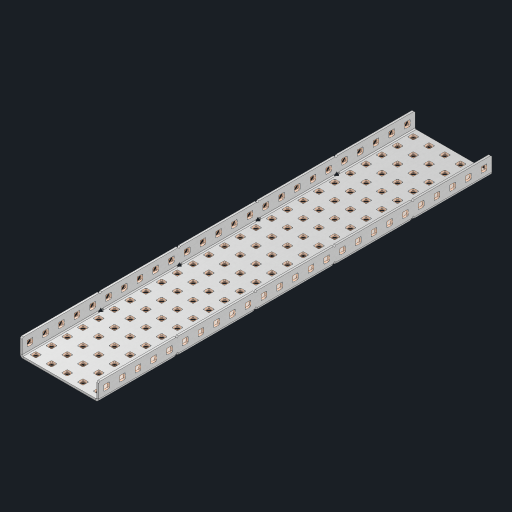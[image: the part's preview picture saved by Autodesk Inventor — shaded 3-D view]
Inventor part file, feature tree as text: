
AUTODESK INVENTOR PART (.ipt)
format: ipt  version: 2023 (Build 270158000, 158)  size: 1,938,432 bytes
history: native  units: in
note: dims shown in document units (in); Inventor stores cm internally (conversion verified against a paired STEP export)
features: other x180, extrude x174, sheet_metal_op x10, sketch x8, mirror x1, pattern_linear x1, chamfer x1
ambient origin geometry x8: Origin, YZ Plane, XZ Plane, XY Plane, X Axis, Y Axis, Z Axis, Center Point
bodies: Solid1 (feature_tree), Body (feature_tree)
feature tree (375):
  other  "Flange Pattern Plane"
  sheet_metal_op  "Flange Pattern"
  sheet_metal_op  "Body Pattern"
  other  "Arc Length"
  mirror  "Notch Mirror"
  pattern_linear  "Notch Pattern"  Spacing1=0.25in  [1 undecoded]
  chamfer  "End Chamfer"
  extrude  "Half Cut"  Depth=0.0625in
  sketch  "Sketch1"  dims[d0=2.5in]
  other  "Plate1"
  sketch  "Sketch2"  dims[d1=12.5in]
  other  "Plate2"
  sheet_metal_op  "Bend1"
  sheet_metal_op  "Corner1"
  sketch  "Sketch3"  dims[d2=0.0625in]
  other  "Flange Pattern Sketch"
  sketch  "Sketch7"  dims[d3=0.0625in]
  other  "Srf1"
  other  "Srf2"
  sketch  "Sketch8"  dims[d4=0.0312in]
  sketch  "Sketch9"  dims[d5=0.125in]
  other  "Srf91"
  sheet_metal_op  "Body Pattern Sketch"
  other  "Srf92"
  sketch  "Sketch13"  dims[d6=0.0625in]
  sketch  "Sketch14"  dims[d7=0.5in d8=90.0deg d9=0.0312in d10=0.25in d11=0.0625in d12=0.0625in d16=0.182in d17=0.02in d18=0.0625in d19=0.0in d20=0.25in d21=0.25in d46=0.172in d47=1.0in d48=0.0in d49=0.182in d50=0.02in d51=0.25in d52=0.25in d53=0.0625in d54=0.0in d55=0.172in d56=1.0in d57=0.0in d60=9.8425in d62=0.5in d63=1.9685in d65=0.5in d85=0.1473in d86=0.1782in d88=0.04in d89=0.0625in d90=0.0in d91=0.04in d92=0.0491in d95=2.5in d96=0.04in d97=0.25in d98=45.0deg d101=0.0in d102=2.497in d131=2.5in d132=9.8425in d134=0.5in d139=0.5in]
  other  "Srf856"
  other  "Srf1310"
  other  "Srf1311"
  other  "Srf1312"
  other  "Srf1376"
  other  "Srf1377"
  other  "Srf1728"
  other  "Srf1755"
  other  "Srf1878"
  other  "Srf1879"
  other  "Srf1880"
  other  "Srf1881"
  other  "Srf1882"
  other  "Srf1883"
  other  "Srf1884"
  other  "Srf1885"
  other  "Srf1886"
  other  "Srf1887"
  other  "Srf1888"
  other  "Srf1889"
  other  "Srf1890"
  other  "Srf1891"
  other  "Srf1892"
  other  "Srf1893"
  other  "Srf1894"
  other  "Srf1895"
  other  "Srf1896"
  other  "Srf1897"
  other  "Srf1898"
  other  "Srf1899"
  other  "Srf1900"
  other  "Srf1901"
  other  "Srf1902"
  other  "Srf1903"
  other  "Srf1904"
  other  "Srf1905"
  other  "Srf1906"
  other  "Srf1942"
  other  "Srf1943"
  other  "Srf1944"
  other  "Srf1945"
  other  "Srf1946"
  other  "Srf1947"
  other  "Srf1948"
  other  "Srf1949"
  other  "Srf1950"
  other  "Srf1951"
  other  "Srf1952"
  other  "Srf1953"
  other  "Srf1954"
  other  "Srf1955"
  other  "Srf1956"
  other  "Srf1957"
  other  "Srf1958"
  other  "Srf1959"
  other  "Srf1960"
  other  "Srf1961"
  other  "Srf1962"
  other  "Srf1963"
  other  "Srf1964"
  other  "Srf1965"
  other  "Srf1966"
  other  "Srf1967"
  other  "Srf1968"
  other  "Srf1969"
  other  "Srf1970"
  other  "Srf2111"
  other  "Srf2112"
  other  "Srf2113"
  other  "Srf2114"
  other  "Srf2115"
  other  "Srf2116"
  other  "Srf2117"
  other  "Srf2118"
  other  "Srf2119"
  other  "Srf2120"
  other  "Srf2121"
  other  "Srf2122"
  other  "Srf2123"
  other  "Srf2124"
  other  "Srf2125"
  other  "Srf2146"
  other  "Srf2147"
  other  "Srf2148"
  other  "Srf2149"
  other  "Srf2150"
  other  "Srf2151"
  other  "Srf2152"
  other  "Srf2153"
  other  "Srf2154"
  other  "Srf2155"
  other  "Srf2156"
  other  "Srf2157"
  other  "Srf2158"
  other  "Srf2159"
  other  "Srf2160"
  other  "Srf2161"
  other  "Srf2162"
  other  "Srf2163"
  other  "Srf2164"
  other  "Srf2165"
  other  "Srf2166"
  other  "Srf2167"
  other  "Srf2168"
  other  "Srf2169"
  other  "Srf2170"
  other  "Srf2171"
  other  "Srf2172"
  other  "Srf2173"
  other  "Srf2174"
  other  "Srf2175"
  other  "Srf2176"
  other  "Srf2177"
  other  "Srf2178"
  other  "Srf2179"
  other  "Srf2180"
  other  "Srf2181"
  other  "Srf2182"
  other  "Srf2183"
  other  "Srf2184"
  other  "Srf2185"
  other  "Srf2186"
  other  "Srf2187"
  other  "Srf2188"
  other  "Srf2189"
  other  "Srf2190"
  other  "Srf2191"
  other  "Srf2192"
  other  "Srf2193"
  other  "Srf2194"
  other  "Srf2195"
  other  "Srf2196"
  other  "Srf2197"
  other  "Srf2198"
  other  "Srf2199"
  other  "Srf2200"
  other  "Srf2201"
  other  "Srf2202"
  other  "Srf2203"
  other  "Srf2204"
  other  "Srf2205"
  other  "Srf2206"
  other  "Srf2207"
  other  "Srf2208"
  other  "Srf2209"
  other  "Srf2210"
  other  "Srf2211"
  other  "Srf2212"
  other  "Srf2213"
  other  "Srf2214"
  other  "Srf2215"
  other  "Srf2216"
  other  "Srf2217"
  other  "Srf2218"
  other  "Srf2219"
  other  "Srf2220"
  other  "Srf2221"
  other  "Srf2222"
  other  "Srf2223"
  other  "Srf2224"
  other  "Srf2225"
  other  "Srf2226"
  other  "Srf2227"
  other  "Srf2228"
  other  "Srf2229"
  other  "Srf2230"
  other  "Srf2231"
  other  "Srf2232"
  other  "Srf2233"
  other  "Srf2234"
  other  "Srf2235"
  sheet_metal_op  "Flange Stamp"
  sheet_metal_op  "Flange Circle"
  sheet_metal_op  "Body Stamp"
  sheet_metal_op  "Body Circle"
  sheet_metal_op  "Notch"
  extrude  "ExtrusionSrf2"  Depth=0.0625in
  extrude  "ExtrusionSrf92"  Depth=2.5in
  extrude  "ExtrusionSrf856"  Depth=0.02in
  extrude  "ExtrusionSrf1310"  Depth=0.0625in
  extrude  "ExtrusionSrf1311"  TaperAngle=0.0deg  [1 undecoded]
  extrude  "ExtrusionSrf1312"  Depth=0.25in
  extrude  "ExtrusionSrf1376"  Depth=0.25in
  extrude  "ExtrusionSrf1377"  Depth=2.5in
  extrude  "ExtrusionSrf1728"  Depth=2.5in TaperAngle=0.0deg
  extrude  "ExtrusionSrf1755"  Depth=2.5in
  extrude  "ExtrusionSrf1878"  Depth=0.02in
  extrude  "ExtrusionSrf1879"  Depth=0.25in
  extrude  "ExtrusionSrf1880"  Depth=0.25in
  extrude  "ExtrusionSrf1881"  Depth=0.0625in
  extrude  "ExtrusionSrf1882"  TaperAngle=0.0deg  [1 undecoded]
  extrude  "ExtrusionSrf1883"  Depth=2.5in
  extrude  "ExtrusionSrf1884"  Depth=2.5in TaperAngle=0.0deg
  extrude  "ExtrusionSrf1885"  Depth=2.5in
  extrude  "ExtrusionSrf1886"  Depth=2.5in
  extrude  "ExtrusionSrf1887"  Depth=2.5in
  extrude  "ExtrusionSrf1888"  Depth=2.5in
  extrude  "ExtrusionSrf1889"  Depth=2.5in
  extrude  "ExtrusionSrf1890"  Depth=0.0625in
  extrude  "ExtrusionSrf1891"  TaperAngle=0.0deg  [1 undecoded]
  extrude  "ExtrusionSrf1892"  Depth=2.5in
  extrude  "ExtrusionSrf1893"  Depth=2.5in
  extrude  "ExtrusionSrf1894"  Depth=2.5in
  extrude  "ExtrusionSrf1895"  Depth=0.25in TaperAngle=45.0deg
  extrude  "ExtrusionSrf1896"  TaperAngle=0.0deg  [1 undecoded]
  extrude  "ExtrusionSrf1897"  Depth=2.5in
  extrude  "ExtrusionSrf1898"  Depth=2.5in
  extrude  "ExtrusionSrf1899"  Depth=2.5in
  extrude  "ExtrusionSrf1900"  Depth=2.5in
  extrude  "ExtrusionSrf1901"  Depth=2.5in
  extrude  "ExtrusionSrf1902"  [1 undecoded]
  extrude  "ExtrusionSrf1903"  [1 undecoded]
  extrude  "ExtrusionSrf1904"  [1 undecoded]
  extrude  "ExtrusionSrf1905"  [1 undecoded]
  extrude  "ExtrusionSrf1906"  [1 undecoded]
  extrude  "ExtrusionSrf1942"  [1 undecoded]
  extrude  "ExtrusionSrf1943"  [1 undecoded]
  extrude  "ExtrusionSrf1944"  [1 undecoded]
  extrude  "ExtrusionSrf1945"  [1 undecoded]
  extrude  "ExtrusionSrf1946"  [1 undecoded]
  extrude  "ExtrusionSrf1947"  [1 undecoded]
  extrude  "ExtrusionSrf1948"  [1 undecoded]
  extrude  "ExtrusionSrf1949"  [1 undecoded]
  extrude  "ExtrusionSrf1950"  [1 undecoded]
  extrude  "ExtrusionSrf1951"  [1 undecoded]
  extrude  "ExtrusionSrf1952"  [1 undecoded]
  extrude  "ExtrusionSrf1953"  [1 undecoded]
  extrude  "ExtrusionSrf1954"  [1 undecoded]
  extrude  "ExtrusionSrf1955"  [1 undecoded]
  extrude  "ExtrusionSrf1956"  [1 undecoded]
  extrude  "ExtrusionSrf1957"  [1 undecoded]
  extrude  "ExtrusionSrf1958"  [1 undecoded]
  extrude  "ExtrusionSrf1959"  [1 undecoded]
  extrude  "ExtrusionSrf1960"  [1 undecoded]
  extrude  "ExtrusionSrf1961"  [1 undecoded]
  extrude  "ExtrusionSrf1962"  [1 undecoded]
  extrude  "ExtrusionSrf1963"  [1 undecoded]
  extrude  "ExtrusionSrf1964"  [1 undecoded]
  extrude  "ExtrusionSrf1965"  [1 undecoded]
  extrude  "ExtrusionSrf1966"  [1 undecoded]
  extrude  "ExtrusionSrf1967"  [1 undecoded]
  extrude  "ExtrusionSrf1968"  [1 undecoded]
  extrude  "ExtrusionSrf1969"  [1 undecoded]
  extrude  "ExtrusionSrf1970"  [1 undecoded]
  extrude  "ExtrusionSrf2111"  [1 undecoded]
  extrude  "ExtrusionSrf2112"  [1 undecoded]
  extrude  "ExtrusionSrf2113"  [1 undecoded]
  extrude  "ExtrusionSrf2114"  [1 undecoded]
  extrude  "ExtrusionSrf2115"  [1 undecoded]
  extrude  "ExtrusionSrf2116"  [1 undecoded]
  extrude  "ExtrusionSrf2117"  [1 undecoded]
  extrude  "ExtrusionSrf2118"  [1 undecoded]
  extrude  "ExtrusionSrf2119"  [1 undecoded]
  extrude  "ExtrusionSrf2120"  [1 undecoded]
  extrude  "ExtrusionSrf2121"  [1 undecoded]
  extrude  "ExtrusionSrf2122"  [1 undecoded]
  extrude  "ExtrusionSrf2123"  [1 undecoded]
  extrude  "ExtrusionSrf2124"  [1 undecoded]
  extrude  "ExtrusionSrf2125"  [1 undecoded]
  extrude  "ExtrusionSrf2146"  [1 undecoded]
  extrude  "ExtrusionSrf2147"  [1 undecoded]
  extrude  "ExtrusionSrf2148"  [1 undecoded]
  extrude  "ExtrusionSrf2149"  [1 undecoded]
  extrude  "ExtrusionSrf2150"  [1 undecoded]
  extrude  "ExtrusionSrf2151"  [1 undecoded]
  extrude  "ExtrusionSrf2152"  [1 undecoded]
  extrude  "ExtrusionSrf2153"  [1 undecoded]
  extrude  "ExtrusionSrf2154"  [1 undecoded]
  extrude  "ExtrusionSrf2155"  [1 undecoded]
  extrude  "ExtrusionSrf2156"  [1 undecoded]
  extrude  "ExtrusionSrf2157"  [1 undecoded]
  extrude  "ExtrusionSrf2158"  [1 undecoded]
  extrude  "ExtrusionSrf2159"  [1 undecoded]
  extrude  "ExtrusionSrf2160"  [1 undecoded]
  extrude  "ExtrusionSrf2161"  [1 undecoded]
  extrude  "ExtrusionSrf2162"  [1 undecoded]
  extrude  "ExtrusionSrf2163"  [1 undecoded]
  extrude  "ExtrusionSrf2164"  [1 undecoded]
  extrude  "ExtrusionSrf2165"  [1 undecoded]
  extrude  "ExtrusionSrf2166"  [1 undecoded]
  extrude  "ExtrusionSrf2167"  [1 undecoded]
  extrude  "ExtrusionSrf2168"  [1 undecoded]
  extrude  "ExtrusionSrf2169"  [1 undecoded]
  extrude  "ExtrusionSrf2170"  [1 undecoded]
  extrude  "ExtrusionSrf2171"  [1 undecoded]
  extrude  "ExtrusionSrf2172"  [1 undecoded]
  extrude  "ExtrusionSrf2173"  [1 undecoded]
  extrude  "ExtrusionSrf2174"  [1 undecoded]
  extrude  "ExtrusionSrf2175"  [1 undecoded]
  extrude  "ExtrusionSrf2176"  [1 undecoded]
  extrude  "ExtrusionSrf2177"  [1 undecoded]
  extrude  "ExtrusionSrf2178"  [1 undecoded]
  extrude  "ExtrusionSrf2179"  [1 undecoded]
  extrude  "ExtrusionSrf2180"  [1 undecoded]
  extrude  "ExtrusionSrf2181"  [1 undecoded]
  extrude  "ExtrusionSrf2182"  [1 undecoded]
  extrude  "ExtrusionSrf2183"  [1 undecoded]
  extrude  "ExtrusionSrf2184"  [1 undecoded]
  extrude  "ExtrusionSrf2185"  [1 undecoded]
  extrude  "ExtrusionSrf2186"  [1 undecoded]
  extrude  "ExtrusionSrf2187"  [1 undecoded]
  extrude  "ExtrusionSrf2188"  [1 undecoded]
  extrude  "ExtrusionSrf2189"  [1 undecoded]
  extrude  "ExtrusionSrf2190"  [1 undecoded]
  extrude  "ExtrusionSrf2191"  [1 undecoded]
  extrude  "ExtrusionSrf2192"  [1 undecoded]
  extrude  "ExtrusionSrf2193"  [1 undecoded]
  extrude  "ExtrusionSrf2194"  [1 undecoded]
  extrude  "ExtrusionSrf2195"  [1 undecoded]
  extrude  "ExtrusionSrf2196"  [1 undecoded]
  extrude  "ExtrusionSrf2197"  [1 undecoded]
  extrude  "ExtrusionSrf2198"  [1 undecoded]
  extrude  "ExtrusionSrf2199"  [1 undecoded]
  extrude  "ExtrusionSrf2200"  [1 undecoded]
  extrude  "ExtrusionSrf2201"  [1 undecoded]
  extrude  "ExtrusionSrf2202"  [1 undecoded]
  extrude  "ExtrusionSrf2203"  [1 undecoded]
  extrude  "ExtrusionSrf2204"  [1 undecoded]
  extrude  "ExtrusionSrf2205"  [1 undecoded]
  extrude  "ExtrusionSrf2206"  [1 undecoded]
  extrude  "ExtrusionSrf2207"  [1 undecoded]
  extrude  "ExtrusionSrf2208"  [1 undecoded]
  extrude  "ExtrusionSrf2209"  [1 undecoded]
  extrude  "ExtrusionSrf2210"  [1 undecoded]
  extrude  "ExtrusionSrf2211"  [1 undecoded]
  extrude  "ExtrusionSrf2212"  [1 undecoded]
  extrude  "ExtrusionSrf2213"  [1 undecoded]
  extrude  "ExtrusionSrf2214"  [1 undecoded]
  extrude  "ExtrusionSrf2215"  [1 undecoded]
  extrude  "ExtrusionSrf2216"  [1 undecoded]
  extrude  "ExtrusionSrf2217"  [1 undecoded]
  extrude  "ExtrusionSrf2218"  [1 undecoded]
  extrude  "ExtrusionSrf2219"  [1 undecoded]
  extrude  "ExtrusionSrf2220"  [1 undecoded]
  extrude  "ExtrusionSrf2221"  [1 undecoded]
  extrude  "ExtrusionSrf2222"  [1 undecoded]
  extrude  "ExtrusionSrf2223"  [1 undecoded]
  extrude  "ExtrusionSrf2224"  [1 undecoded]
  extrude  "ExtrusionSrf2225"  [1 undecoded]
  extrude  "ExtrusionSrf2226"  [1 undecoded]
  extrude  "ExtrusionSrf2227"  [1 undecoded]
  extrude  "ExtrusionSrf2228"  [1 undecoded]
  extrude  "ExtrusionSrf2229"  [1 undecoded]
  extrude  "ExtrusionSrf2230"  [1 undecoded]
  extrude  "ExtrusionSrf2231"  [1 undecoded]
  extrude  "ExtrusionSrf2232"  [1 undecoded]
  extrude  "ExtrusionSrf2233"  [1 undecoded]
  extrude  "ExtrusionSrf2234"  [1 undecoded]
  extrude  "ExtrusionSrf2235"  [1 undecoded]
note: 144 required parameter values undecoded (feature->parameter linkage not recoverable at this tier; creation-order binding heuristic only, values carry confidence <= 0.55)
